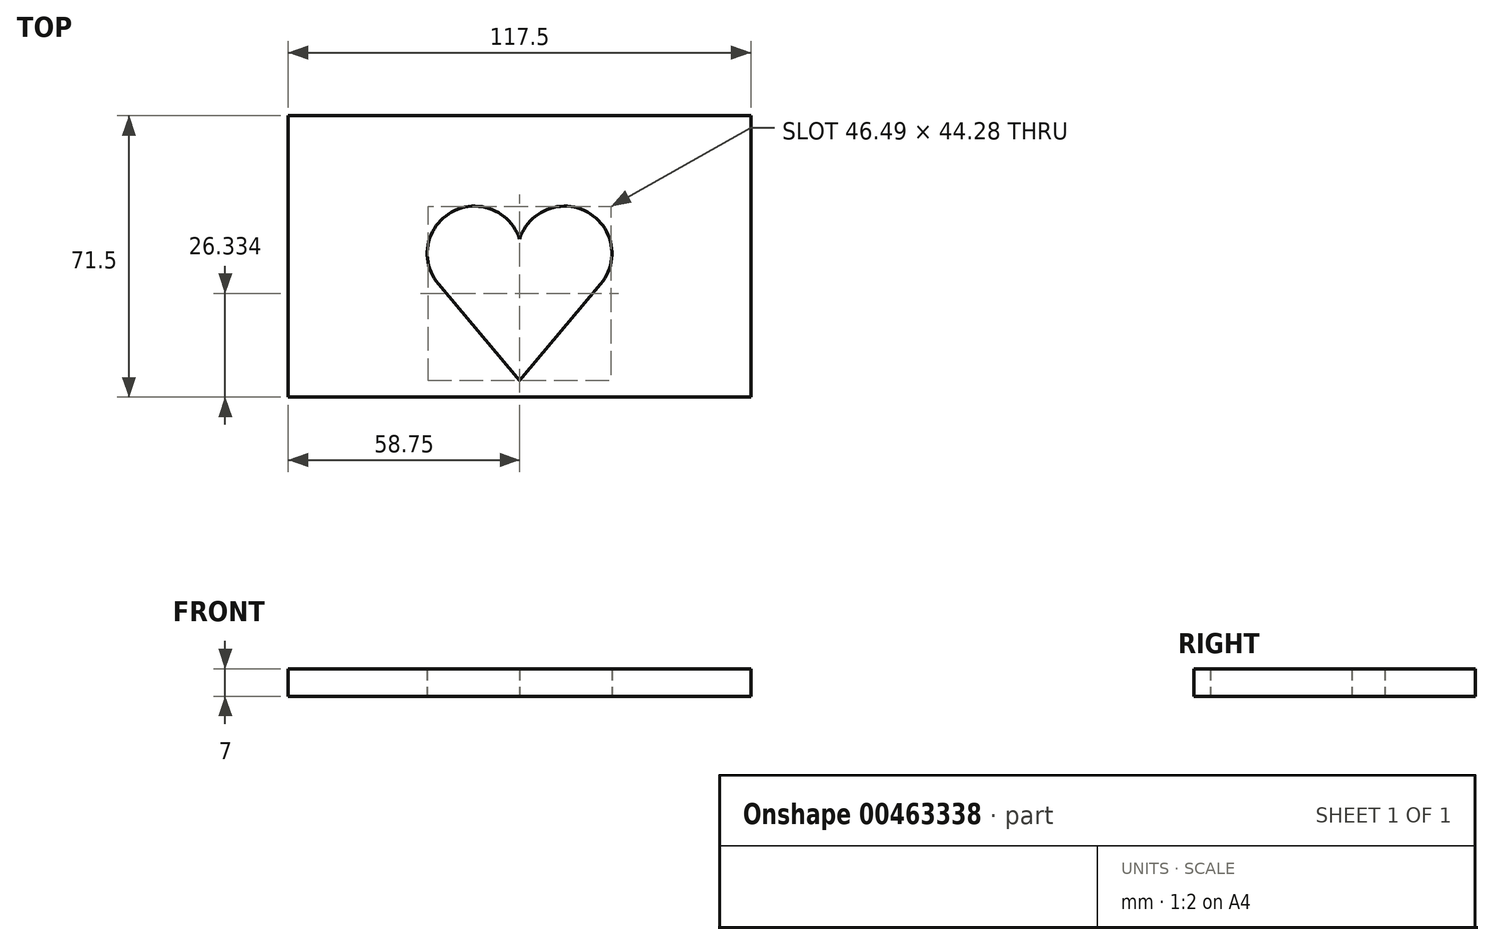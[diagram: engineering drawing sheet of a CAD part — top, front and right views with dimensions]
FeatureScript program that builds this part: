
annotation { "Feature Type Name" : "Feature", "Feature Type Description" : "" }
export const myFeature = defineFeature(function(context is Context, id is Id, definition is map)
    precondition{}
    {
        {
            var Q0;
            Q0=qCreatedBy(makeId("Top.planeOp"),FACE);
            var sketch = newSketch(context, id + "F0", { "sketchPlane" : qUnion([Q0])});
            skLineSegment(sketch, "E0.bottom", {"start": v(58.75, -35.75) * mm, "end": v(-58.75, -35.75) * mm});
            skLineSegment(sketch, "E0.top", {"start": v(58.75, 35.75) * mm, "end": v(-58.75, 35.75) * mm});
            skLineSegment(sketch, "E0.left", {"start": v(58.75, -35.75) * mm, "end": v(58.75, 35.75) * mm});
            skLineSegment(sketch, "E0.right", {"start": v(-58.75, -35.75) * mm, "end": v(-58.75, 35.75) * mm});
            skPoint(sketch, "E0.middle", {"position": v(0, 0) * mm});
            skLineSegment(sketch, "E1", {"start": v(0, -31.56) * mm, "end": v(20.63, -6.99) * mm});
            skArc(sketch, "E2", {"start": v(20.63, -6.99) * mm, "mid": v(17.24, 11.25) * mm, "end": v(0, 4.4) * mm});
            skLineSegment(sketch, "E3.MirrorCS", {"start": v(0, -31.56) * mm, "end": v(-20.63, -6.99) * mm});
            skArc(sketch, "E4.MirrorCS", {"start": v(-20.63, -6.99) * mm, "mid": v(-17.24, 11.25) * mm, "end": v(0, 4.4) * mm});
            skSolve(sketch);
        }
        {
            var Q0;
            Q0=makeQuery(id+"F0.imprint","IMPRINT",FACE,{"disambiguationData":[TD([[makeQuery(id+"F0.imprint","IMPRINT",EDGE,{"derivedFrom":sQuery(id+"F0.wireOp",EDGE,"E0.bottom")}),-1.0]])]});
            extrude(context, id + "F1", {"entities" : qUnion([Q0]), "depth" : 7 * mm});
        }
    });
